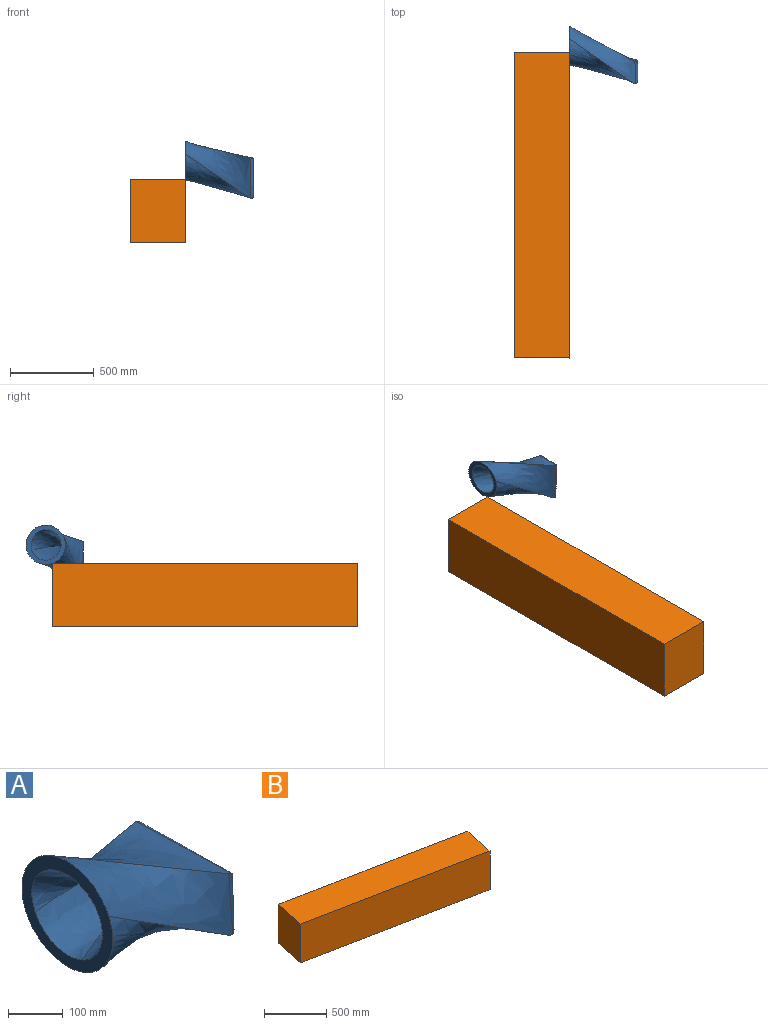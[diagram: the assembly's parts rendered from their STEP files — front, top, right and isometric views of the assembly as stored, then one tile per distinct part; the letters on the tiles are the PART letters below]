
ASSEMBLY  parts=2 mates=1
PART A: 15 faces, bbox 478.3x407.1x414.7 mm
  f0: plane 242.06x242.06mm, normal (-1,0,0), area 17806.8mm2, adj f2,f3,f4,f5,f7,f8,f9,f10
  f1: plane 220.23x110.22mm, normal (1,0,0), area 22815.8mm2, adj f11,f12,f13,f14
  f2: bspline ~407.04x254.22mm, area 79687.8mm2, adj f0,f3,f5,f11,f13,f14
  f3: bspline ~407.04x356.58mm, area 60978.5mm2, adj f0,f2,f4,f11,f12
  f4: bspline ~388.46x326.62mm, area 75927.4mm2, adj f0,f3,f5,f12,f14
  f5: bspline ~417.17x278.11mm, area 58962.3mm2, adj f0,f2,f4,f14
  f6: plane 198.36x91.43mm, normal (-1,0,0), area 15128.4mm2, adj f7,f8,f9,f10
  f7: offset ~475.91x308.96mm, area 59854.9mm2, adj f0,f6,f8,f10
  f8: offset ~457.83x407.38mm, area 39474.4mm2, adj f0,f6,f7,f9
  f9: offset ~472.37x398.43mm, area 58411mm2, adj f0,f6,f8,f10
  f10: offset ~473.86x332.84mm, area 39859.4mm2, adj f0,f6,f7,f9
  f11: bspline ~144.27x19.71mm, area 2612.7mm2, adj f1,f2,f3,f12,f13
  f12: bspline ~259.57x27.88mm, area 6628.8mm2, adj f1,f3,f4,f11,f14
  f13: bspline ~271.38x16.99mm, area 4086.4mm2, adj f1,f2,f11,f14
  f14: bspline ~146.83x27.84mm, area 3602.8mm2, adj f1,f2,f4,f5,f12,f13
PART B: 6 faces, bbox 1857.7x678.9x381 mm
  f0: plane 1857.67x678.89mm, normal (0,0,-1), area 606086.2mm2, adj f1,f3,f4,f5
  f1: plane 381x325.28mm, normal (0.98,-0.19,0), area 126319.1mm2, adj f0,f2,f4,f5
  f2: plane 1857.67x678.89mm, normal (0,0,1), area 606086.2mm2, adj f1,f3,f4,f5
  f3: plane 381x325.28mm, normal (-0.98,0.19,0), area 126319.1mm2, adj f0,f2,f4,f5
  f4: plane 1793.53x381mm, normal (-0.19,-0.98,0), area 696490.7mm2, adj f0,f1,f2,f3
  f5: plane 1793.53x381mm, normal (0.19,0.98,0), area 696490.7mm2, adj f0,f1,f2,f3
PLACE A rot(axis=(-1,0,0),86deg) t=(52.27,184.62,110.69)mm
PLACE B rot(axis=(0,0,-1),78.8deg) t=(1458.76,450.51,-174.7)mm fixed
MATE revolute B.f5 <-> A.f0  axis (1,0,0) through (52.27,158.04,15.8)mm
